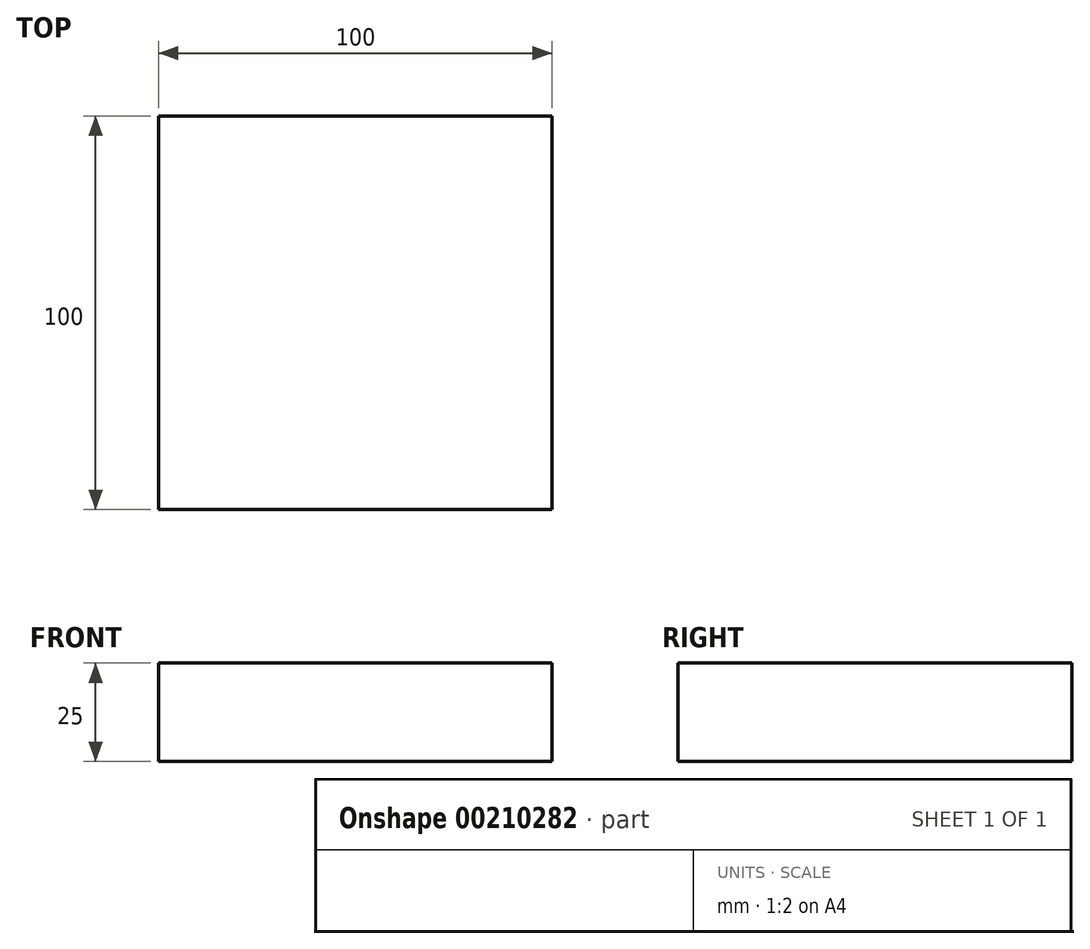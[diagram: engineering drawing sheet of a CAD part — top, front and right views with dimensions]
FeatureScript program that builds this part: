
annotation { "Feature Type Name" : "Feature", "Feature Type Description" : "" }
export const myFeature = defineFeature(function(context is Context, id is Id, definition is map)
    precondition{}
    {
        {
            var Q0;
            Q0=qCreatedBy(makeId("Front.planeOp"),FACE);
            var sketch = newSketch(context, id + "F0", { "sketchPlane" : qUnion([Q0])});
            skLineSegment(sketch, "E0.bottom", {"start": v(0, 0) * mm, "end": v(100, 0) * mm});
            skLineSegment(sketch, "E0.top", {"start": v(0, 25) * mm, "end": v(100, 25) * mm});
            skLineSegment(sketch, "E0.left", {"start": v(0, 0) * mm, "end": v(0, 25) * mm});
            skLineSegment(sketch, "E0.right", {"start": v(100, 0) * mm, "end": v(100, 25) * mm});
            skSolve(sketch);
        }
        {
            var Q0;
            Q0=makeQuery(id+"F0.imprint","IMPRINT",FACE,{"disambiguationData":[TD([[makeQuery(id+"F0.imprint","IMPRINT",EDGE,{"derivedFrom":sQuery(id+"F0.wireOp",EDGE,"E0.bottom")}),1.0]])]});
            extrude(context, id + "F1", {"entities" : qUnion([Q0]), "endBound" : BoundingType.SYMMETRIC, "oppositeDirection" : true, "depth" : 100 * mm});
        }
    });
